# Revit family: QF_ELECTROLUXPROFESSIONAL_1L059Z_TD6-20_S
name_source: partatom
category: Attrezzature speciali
units: mm (PartAtom-declared; Revit-internal decimal feet)

## family parameters
Basato su piano di lavoro = No
Condiviso = No
Punto di calcolo locali = No
Quota connettore circolare = Usa diametro
Sempre verticale = Sì
Taglio con vuoti quando caricato = No
Tipo di parte = Normale

## types (18) — shared parameters
Height Actual = 1771 mm  [stored 5.81037 ft]
Latent Heat Output = 0.0
Length Actual = 790 mm  [stored 2.59186 ft]
Modello = TD6-20
Produttore = Electrolux Professional
Sensible Heat Output = 0.0
URL = www.electroluxprofessional.com
zero-valued in all types: Gas KW, Prospetto di default, Steam Pounds per Hour

## per-type parameters (varying)
| type | Cycle | Depth Actual | Descrizione | Item Number | Phase | Volts | Watts | Weight |
| 9873830062 | 60 Hz | 1342 mm  [stored 4.40289 ft] | TUMBLE DRYER TD6-20 20KG GALVA.DRUM STEAM 25KW 208-240/60/1 COMPASS PRO 6G82 EU SILVER DO.RIGHT STOP DISCON. EXT.CONN. | 1L0EHB | 1 | 240 V | 1200 W | 250 |
| 9873830303 | 50 Hz | 1202 mm  [stored 3.94357 ft] | TUMBLE DRYER TD6-20 20KG SST DRUM STEAM 25KW 400/50/3 COMPASS PRO 6G81 EU SILVER DO.RIGHT MB DSC STOP DISCON. | 1LT6HZ | 3 | 400 V | 1000 W | 243 |
| 9873830262 | 60 Hz | 1202 mm  [stored 3.94357 ft] | TUMBLE DRYER TD6-20 20KG GALVA.DRUM STEAM 25KW 208-240/60/1 COMPASS PRO 6G82 EU SST DO.RIGHT STOP DISCON. | 1LSPS0 | 1 | 240 V | 1200 W | 243 |
| 9873830198 | 50 Hz | 1342 mm  [stored 4.40289 ft] | TUMBLE DRYER TD6-20 20KG SST DRUM STEAM 25KW 400/50/3N COMPASS PRO 6G81 SE SILVER DO.LEFT.INS. MB DSC STOP DISCON. | 1LSNZW | 3 | 400 V | 1000 W | 250 |
| 9873830188 | 60 Hz | 1342 mm  [stored 4.40289 ft] | TUMBLE DRYER TD6-20 20KG GALVA.DRUM STEAM 25KW 240/60/1N COMPASS PRO 6G81 EU SILVER DO.RIGHT MB STOP DISCON. | 1LSNVA | 1 | 240 V | 1200 W | 250 |
| 9873830115 | 50 Hz | 1342 mm  [stored 4.40289 ft] | TUMBLE DRYER TD6-20 20KG GALVA.DRUM STEAM 25KW 400/50/3N COMPASS PRO 6G81 EU SILVER DO.RIGHT MB STOP DISCON. | 1LSN63 | 3 | 400 V | 1000 W | 250 |
| 9873830145 | 50 Hz | 1342 mm  [stored 4.40289 ft] | TUMBLE DRYER TD6-20 20KG SST DRUM STEAM 25KW 230/50/3 COMPASS PRO 6G81 EU SILVER DO.LEFT MB STOP DISCON. | 1LSNDX | 3 | 230 V | 1000 W | 250 |
| 9873830064 | 60 Hz | 1342 mm  [stored 4.40289 ft] | TUMBLE DRYER TD6-20 20KG SST DRUM STEAM 25KW 208-240/60/1 COMPASS PRO 6G82 EU SST DO.RIGHT.INS. STOP DISCON. EXT.CONN. | 1LSN3U | 1 | 240 V | 1200 W | 250 |
| 9873830255 | 60 Hz | 1202 mm  [stored 3.94357 ft] | TUMBLE DRYER TD6-20 MARINE 20KG GALVA.DRUM STEAM 25KW 440/60/3 COMPASS PRO 6G81 SE SST/SILVER DO.RIGHT MB STOP DISCON. E | 1L0H12 | 3 | 440 V | 1000 W | 243 |
| 9873830280 | 60 Hz | 1202 mm  [stored 3.94357 ft] | TUMBLE DRYER TD6-20 20KG SST DRUM STEAM 25KW 200/60/3 COMPASS PRO 6G86 JP SST/SILVER DO.RIGHT DISCON. | 1L0H83 | 3 | 200 V | 1000 W | 243 |
| 9873830167 | 50 Hz | 1342 mm  [stored 4.40289 ft] | TUMBLE DRYER TD6-20 20KG GALVA.DRUM STEAM 25KW 240/50/1N COMPASS PRO 6G82 EU SILVER DO.RIGHT STOP DISCON. | 1L0FY3 | 1 | 240 V | 1200 W | 250 |
| 9873830223 | 60 Hz | 1342 mm  [stored 4.40289 ft] | TUMBLE DRYER TD6-20 20KG SST DRUM STEAM 25KW 208-240/60/1 COMPASS PRO 6G81 EU SILVER DO.LEFT MB STOP DISCON. | 1L0GK7 | 1 | 240 V | 1200 W | 250 |
| 9873830056 | 50 Hz | 1342 mm  [stored 4.40289 ft] | TUMBLE DRYER TD6-20 20KG SST DRUM STEAM 25KW 400/50/3 COMPASS PRO 6G81 EU SILVER DO.RIGHT MB STOP DISCON. | 1L0EGY | 3 | 400 V | 1000 W | 250 |
| 9873830154 | 60 Hz | 1342 mm  [stored 4.40289 ft] | TUMBLE DRYER TD6-20 MARINE 20KG GALVA.DRUM STEAM 25KW 440/60/3 COMPASS PRO 6G81 EU SILVER DO.RIGHT MB STOP DISCON. | 1L0FUX | 3 | 440 V | 1000 W | 250 |
| 9873830279 | 50 Hz | 1202 mm  [stored 3.94357 ft] | TUMBLE DRYER TD6-20 20KG SST DRUM STEAM 25KW 200/50/3 COMPASS PRO 6G86 JP SST/SILVER DO.RIGHT DISCON. | 1L0H82 | 3 | 200 V | 1000 W | 243 |
| 9873830146 | 50 Hz | 1342 mm  [stored 4.40289 ft] | TUMBLE DRYER TD6-20 20KG GALVA.DRUM STEAM 25KW 400/50/3N COMPASS PRO 6G81 EU SST/SILVER DO.RIGHT.INS. MB STOP DISCON. | 1LSNEL | 3 | 400 V | 1000 W | 250 |
| 9873830058 | 60 Hz | 1342 mm  [stored 4.40289 ft] | TUMBLE DRYER TD6-20 20KG GALVA.DRUM STEAM 25KW 208-240/60/1 COMPASS PRO 6G82 EU SILVER DO.RIGHT STOP DISCON. | 1L0EH7 | 1 | 240 V | 1200 W | 250 |
| 9873830133 | 50 Hz | 1342 mm  [stored 4.40289 ft] | TUMBLE DRYER TD6-20 20KG SST DRUM STEAM 25KW 400/50/3N COMPASS PRO 6G81 EU SST DO.LEFT MB STOP DISCON. | 1L0EMV | 3 | 400 V | 1000 W | 250 |

note: [stored X ft] marks values corroborated as IEEE doubles in the binary element streams (Revit-internal decimal feet)

## geometry (parser evidence)
native form markers: Blend x6
no freeform markers — native parametric forms only
